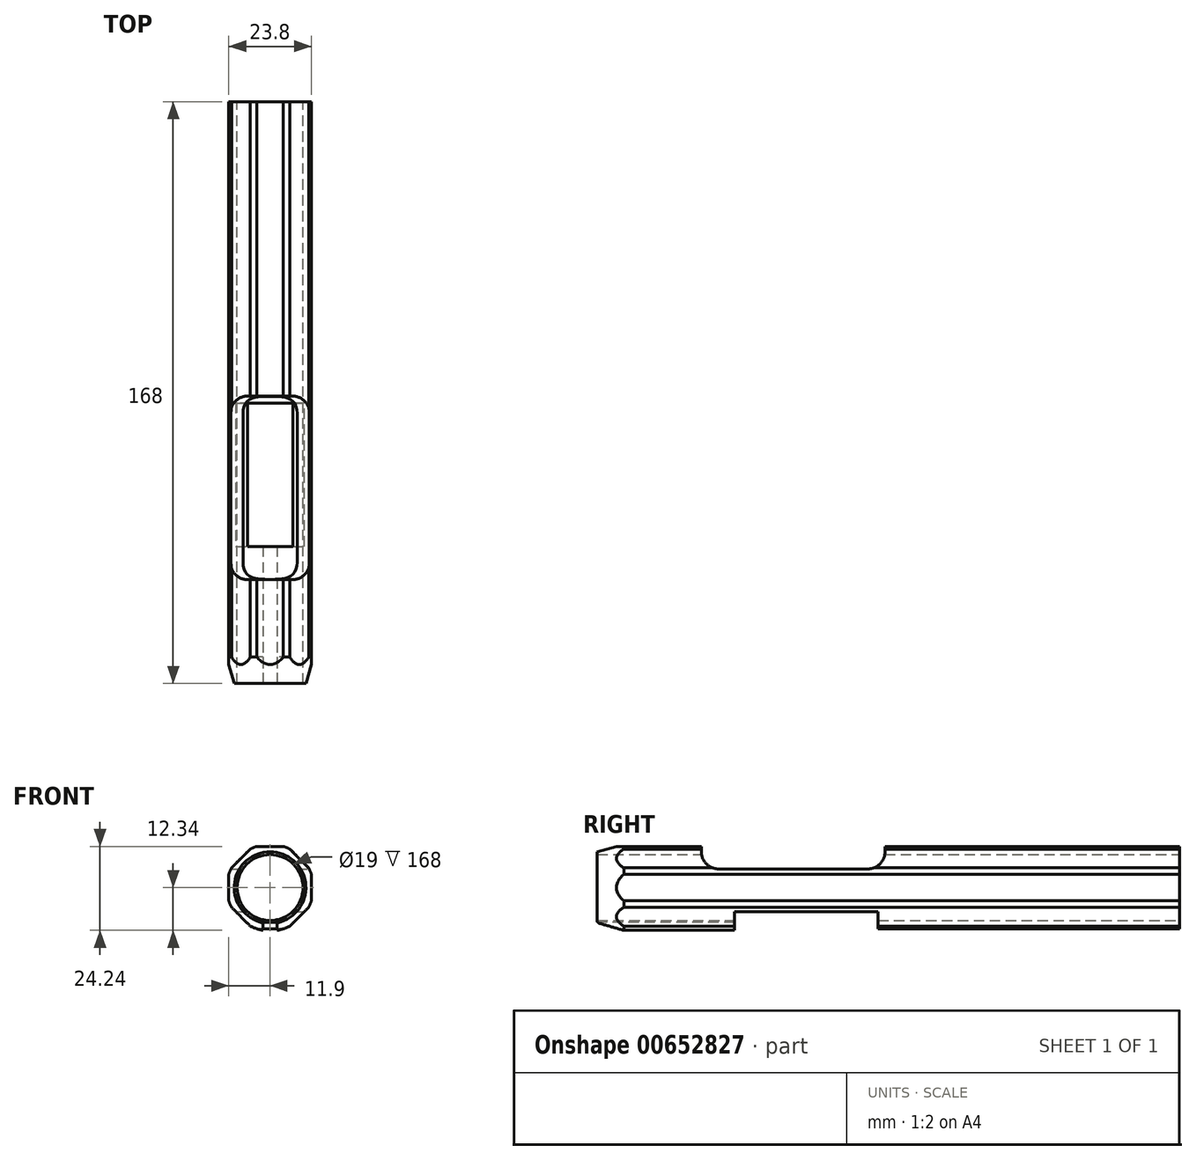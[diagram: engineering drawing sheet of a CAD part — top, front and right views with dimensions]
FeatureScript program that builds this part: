
annotation { "Feature Type Name" : "Feature", "Feature Type Description" : "" }
export const myFeature = defineFeature(function(context is Context, id is Id, definition is map)
    precondition{}
    {
        {
            var Q0;
            Q0=qCreatedBy(makeId("Front.planeOp"),FACE);
            var sketch = newSketch(context, id + "F0", { "sketchPlane" : qUnion([Q0])});
            skArc(sketch, "E0", {"start": v(-11.9, -3.84) * mm, "mid": v(-11.55, -4.78) * mm, "end": v(-11.13, -5.7) * mm});
            skLineSegment(sketch, "E1.0", {"start": v(11.9, 3.84) * mm, "end": v(11.9, -3.84) * mm});
            skLineSegment(sketch, "E1.1", {"start": v(11.13, -5.7) * mm, "end": v(5.7, -11.13) * mm});
            skLineSegment(sketch, "E1.2", {"start": v(3.84, -11.9) * mm, "end": v(-3.84, -11.9) * mm});
            skLineSegment(sketch, "E1.3", {"start": v(-5.7, -11.13) * mm, "end": v(-11.13, -5.7) * mm});
            skLineSegment(sketch, "E1.4", {"start": v(-11.9, -3.84) * mm, "end": v(-11.9, 3.84) * mm});
            skLineSegment(sketch, "E1.5", {"start": v(-11.13, 5.7) * mm, "end": v(-5.7, 11.13) * mm});
            skLineSegment(sketch, "E1.6", {"start": v(-3.84, 11.9) * mm, "end": v(3.84, 11.9) * mm});
            skLineSegment(sketch, "E1.7", {"start": v(5.7, 11.13) * mm, "end": v(11.13, 5.7) * mm});
            skPoint(sketch, "E1.0.midPoint", {"position": v(11.9, 0) * mm});
            skPoint(sketch, "E2.orphan", {"position": v(11.9, 4.93) * mm});
            skPoint(sketch, "E3.orphan", {"position": v(11.9, -4.93) * mm});
            skArc(sketch, "E4.trimOffspring", {"start": v(-11.13, 5.7) * mm, "mid": v(-11.55, 4.78) * mm, "end": v(-11.9, 3.84) * mm});
            skArc(sketch, "E5.trimOffspring", {"start": v(-3.84, 11.9) * mm, "mid": v(-4.78, 11.55) * mm, "end": v(-5.7, 11.13) * mm});
            skArc(sketch, "E6.trimOffspring", {"start": v(5.7, 11.13) * mm, "mid": v(4.78, 11.55) * mm, "end": v(3.84, 11.9) * mm});
            skArc(sketch, "E7.trimOffspring", {"start": v(11.9, 3.84) * mm, "mid": v(11.55, 4.78) * mm, "end": v(11.13, 5.7) * mm});
            skArc(sketch, "E8.trimOffspring", {"start": v(11.13, -5.7) * mm, "mid": v(11.55, -4.78) * mm, "end": v(11.9, -3.84) * mm});
            skArc(sketch, "E9.trimOffspring", {"start": v(3.84, -11.9) * mm, "mid": v(4.78, -11.55) * mm, "end": v(5.7, -11.13) * mm});
            skArc(sketch, "E10.trimOffspring", {"start": v(-5.7, -11.13) * mm, "mid": v(-4.78, -11.55) * mm, "end": v(-3.84, -11.9) * mm});
            skCircle(sketch, "E11", {"center": v(0, 0) * mm, "radius": 9.5 * mm});
            skSolve(sketch);
        }
        {
            var Q0;
            Q0 = qSketchRegion(id + "F0", true);
            extrude(context, id + "F1", {"entities" : qUnion([Q0]), "endBound" : BoundingType.SYMMETRIC, "depth" : 168 * mm, "offsetDistance" : 25 * mm});
        }
        {
            var Q0;
            Q0=qCreatedBy(makeId("Right.planeOp"),FACE);
            var sketch = newSketch(context, id + "F2", { "sketchPlane" : qUnion([Q0])});
            skLineSegment(sketch, "E12.0", {"start": v(-84, 11.13) * mm, "end": v(-84, 5.7) * mm, "construction": true});
            skLineSegment(sketch, "E13", {"start": v(-84, 11.13) * mm, "end": v(-84, -33.45) * mm, "construction": true});
            skLineSegment(sketch, "E14", {"start": v(-84, -33.45) * mm, "end": v(-84, 32.17) * mm, "construction": true});
            skLineSegment(sketch, "E15.bottom", {"start": v(-54, 23.3) * mm, "end": v(-1, 23.3) * mm});
            skLineSegment(sketch, "E15.top", {"start": v(-49, 5.4) * mm, "end": v(-6, 5.4) * mm});
            skLineSegment(sketch, "E15.left", {"start": v(-54, 23.3) * mm, "end": v(-54, 10.4) * mm});
            skLineSegment(sketch, "E15.right", {"start": v(-1, 23.3) * mm, "end": v(-1, 10.4) * mm});
            skLineSegment(sketch, "E16.0", {"start": v(-84, 11.9) * mm, "end": v(84, 11.9) * mm, "construction": true});
            skPoint(sketch, "E17", {"position": v(-54, 11.9) * mm});
            skPoint(sketch, "E18", {"position": v(-1, 11.9) * mm});
            skPoint(sketch, "E19.visualSharp", {"position": v(-54, 5.4) * mm});
            skArc(sketch, "E19.filletArc", {"start": v(-54, 10.4) * mm, "mid": v(-52.54, 6.86) * mm, "end": v(-49, 5.4) * mm});
            skPoint(sketch, "E20.visualSharp", {"position": v(-1, 5.4) * mm});
            skArc(sketch, "E20.filletArc", {"start": v(-6, 5.4) * mm, "mid": v(-2.46, 6.86) * mm, "end": v(-1, 10.4) * mm});
            skSolve(sketch);
        }
        {
            var Q0;
            Q0 = qSketchRegion(id + "F2", true);
            extrude(context, id + "F3", {"entities" : qUnion([Q0]), "operationType" : NewBodyOperationType.REMOVE, "endBound" : BoundingType.SYMMETRIC, "oppositeDirection" : true, "depth" : 25 * mm, "offsetDistance" : 25 * mm});
        }
        {
            var Q0;
            Q0=qCreatedBy(makeId("Right.planeOp"),FACE);
            var sketch = newSketch(context, id + "F4", { "sketchPlane" : qUnion([Q0])});
            skLineSegment(sketch, "E21.0", {"start": v(-84, -11.9) * mm, "end": v(84, -11.9) * mm, "construction": true});
            skLineSegment(sketch, "E22.0", {"start": v(-84, -5.7) * mm, "end": v(-84, -11.13) * mm, "construction": true});
            skLineSegment(sketch, "E23.0", {"start": v(-84, -11.9) * mm, "end": v(-84, -11.13) * mm, "construction": true});
            skLineSegment(sketch, "E24", {"start": v(-44.4, -11.9) * mm, "end": v(-44.4, -23.5) * mm});
            skPoint(sketch, "E25", {"position": v(-44.4, -11.9) * mm});
            skLineSegment(sketch, "E26", {"start": v(-44.4, -11.9) * mm, "end": v(-44.4, -6.9) * mm});
            skLineSegment(sketch, "E27", {"start": v(-44.4, -6.9) * mm, "end": v(-3, -6.9) * mm});
            skLineSegment(sketch, "E28", {"start": v(-3, -6.9) * mm, "end": v(-3, -23.5) * mm});
            skLineSegment(sketch, "E29", {"start": v(-3, -23.5) * mm, "end": v(-44.4, -23.5) * mm});
            skSolve(sketch);
        }
        {
            var Q0;
            Q0 = qSketchRegion(id + "F4", true);
            extrude(context, id + "F5", {"entities" : qUnion([Q0]), "operationType" : NewBodyOperationType.REMOVE, "endBound" : BoundingType.SYMMETRIC, "oppositeDirection" : true, "depth" : 25 * mm, "offsetDistance" : 25 * mm});
        }
        {
            var Q0;
            Q0=makeQuery(id+"F1.opExtrude","CAP_FACE",FACE,{"disambiguationData":[OSD([sQuery(id+"F0.wireOp",EDGE,"E0"),sQuery(id+"F0.wireOp",EDGE,"E1.0"),sQuery(id+"F0.wireOp",EDGE,"E1.1"),sQuery(id+"F0.wireOp",EDGE,"E1.2"),sQuery(id+"F0.wireOp",EDGE,"E1.3"),sQuery(id+"F0.wireOp",EDGE,"E1.4"),sQuery(id+"F0.wireOp",EDGE,"E1.5"),sQuery(id+"F0.wireOp",EDGE,"E1.6"),sQuery(id+"F0.wireOp",EDGE,"E1.7"),sQuery(id+"F0.wireOp",EDGE,"E4.trimOffspring"),sQuery(id+"F0.wireOp",EDGE,"E5.trimOffspring"),sQuery(id+"F0.wireOp",EDGE,"E6.trimOffspring"),sQuery(id+"F0.wireOp",EDGE,"E7.trimOffspring"),sQuery(id+"F0.wireOp",EDGE,"E8.trimOffspring"),sQuery(id+"F0.wireOp",EDGE,"E9.trimOffspring"),sQuery(id+"F0.wireOp",EDGE,"E10.trimOffspring"),sQuery(id+"F0.wireOp",EDGE,"E11")])],"isStart":false});
            cPlane(context, id + "F6", {"entities" : qUnion([Q0]), "cplaneType" : CPlaneType.OFFSET, "offset" : 0 * mm, "width" : 150 * mm, "height" : 150 * mm});
        }
        {
            var Q0;
            Q0=qCreatedBy(id+"F6.planeOp",FACE);
            var sketch = newSketch(context, id + "F7", { "sketchPlane" : qUnion([Q0])});
            skLineSegment(sketch, "E30.0", {"start": v(3.84, -11.9) * mm, "end": v(-3.84, -11.9) * mm, "construction": true});
            skCircle(sketch, "E31.0", {"center": v(0, 0) * mm, "radius": 9.5 * mm, "construction": true});
            skLineSegment(sketch, "E32.bottom", {"start": v(-2, -10) * mm, "end": v(2, -10) * mm});
            skLineSegment(sketch, "E32.top", {"start": v(-2, -13.8) * mm, "end": v(2, -13.8) * mm});
            skLineSegment(sketch, "E32.left", {"start": v(-2, -10) * mm, "end": v(-2, -13.8) * mm});
            skLineSegment(sketch, "E32.right", {"start": v(2, -10) * mm, "end": v(2, -13.8) * mm});
            skPoint(sketch, "E32.middle", {"position": v(0, -11.9) * mm});
            skArc(sketch, "E33", {"start": v(-3.84, -11.9) * mm, "mid": v(0, -12.5) * mm, "end": v(3.84, -11.9) * mm, "construction": true});
            skArc(sketch, "E34.0", {"start": v(-5.7, -11.13) * mm, "mid": v(-4.78, -11.55) * mm, "end": v(-3.84, -11.9) * mm, "construction": true});
            skPoint(sketch, "E35", {"position": v(0, -12.5) * mm});
            skSolve(sketch);
        }
        {
            var Q0;
            Q0 = qSketchRegion(id + "F7", true);
            extrude(context, id + "F8", {"entities" : qUnion([Q0]), "operationType" : NewBodyOperationType.REMOVE, "oppositeDirection" : true, "depth" : 50.14 * mm, "offsetDistance" : 25 * mm});
        }
        {
            var Q0;
            Q0=qCreatedBy(id+"F6.planeOp",FACE);
            var sketch = newSketch(context, id + "F9", { "sketchPlane" : qUnion([Q0])});
            skLineSegment(sketch, "E36.0", {"start": v(-2, -11.9) * mm, "end": v(-3.84, -11.9) * mm, "construction": true});
            skArc(sketch, "E37.0", {"start": v(-5.7, -11.13) * mm, "mid": v(-4.78, -11.55) * mm, "end": v(-3.84, -11.9) * mm, "construction": true});
            skLineSegment(sketch, "E38.0", {"start": v(-2, -10) * mm, "end": v(-2, -11.9) * mm, "construction": true});
            skLineSegment(sketch, "E39.0", {"start": v(-2, -10) * mm, "end": v(2, -10) * mm, "construction": true});
            skLineSegment(sketch, "E40.0", {"start": v(2, -10) * mm, "end": v(2, -11.9) * mm, "construction": true});
            skLineSegment(sketch, "E41.0", {"start": v(3.84, -11.9) * mm, "end": v(2, -11.9) * mm, "construction": true});
            skArc(sketch, "E42.0", {"start": v(3.84, -11.9) * mm, "mid": v(4.78, -11.55) * mm, "end": v(5.7, -11.13) * mm, "construction": true});
            skArc(sketch, "E43", {"start": v(-3.84, -11.9) * mm, "mid": v(-2.93, -12.15) * mm, "end": v(-2, -12.34) * mm});
            skLineSegment(sketch, "E44", {"start": v(2, -10) * mm, "end": v(2, -12.34) * mm});
            skLineSegment(sketch, "E45", {"start": v(-2, -11.9) * mm, "end": v(-2, -12.34) * mm});
            skLineSegment(sketch, "E46", {"start": v(2, -11.9) * mm, "end": v(3.84, -11.9) * mm});
            skLineSegment(sketch, "E47", {"start": v(-2, -11.9) * mm, "end": v(-3.84, -11.9) * mm});
            skArc(sketch, "E48.trimOffspring", {"start": v(2, -12.34) * mm, "mid": v(2.93, -12.15) * mm, "end": v(3.84, -11.9) * mm});
            skSolve(sketch);
        }
        {
            var Q0;
            Q0 = qSketchRegion(id + "F9", true);
            var Q1;
            Q1=makeQuery(id+"F5.boolean.opBoolean","COPY",FACE,{"derivedFrom":makeQuery(id+"F5.opExtrude","SWEPT_FACE",FACE,{"disambiguationData":[OSD([sQuery(id+"F4.wireOp",EDGE,"E24"),sQuery(id+"F4.wireOp",EDGE,"E26")])]})});
            extrude(context, id + "F10", {"entities" : qUnion([Q0]), "operationType" : NewBodyOperationType.ADD, "endBound" : BoundingType.UP_TO_SURFACE, "oppositeDirection" : true, "depth" : 25 * mm, "endBoundEntityFace" : qUnion([Q1]), "offsetDistance" : 25 * mm});
        }
        {
            var Q0;
            Q0=qCreatedBy(makeId("Right.planeOp"),FACE);
            var sketch = newSketch(context, id + "F11", { "sketchPlane" : qUnion([Q0])});
            skLineSegment(sketch, "E49.0.0", {"start": v(-44.4, -12.34) * mm, "end": v(-44.4, -11.13) * mm, "construction": true});
            skLineSegment(sketch, "E49.0.1", {"start": v(-44.4, -11.13) * mm, "end": v(-84, -11.13) * mm, "construction": true});
            skLineSegment(sketch, "E49.0.2", {"start": v(-84, -11.13) * mm, "end": v(-84, -12.34) * mm, "construction": true});
            skLineSegment(sketch, "E49.0.3", {"start": v(-84, -12.34) * mm, "end": v(-44.4, -12.34) * mm, "construction": true});
            skLineSegment(sketch, "E50", {"start": v(-84, -12.34) * mm, "end": v(-81.5, -12.34) * mm});
            skLineSegment(sketch, "E51", {"start": v(-84, -12.34) * mm, "end": v(-84, -9.84) * mm});
            skLineSegment(sketch, "E52", {"start": v(-84, -9.84) * mm, "end": v(-81.5, -12.34) * mm});
            skLineSegment(sketch, "E53", {"start": v(-81.5, -12.34) * mm, "end": v(-84, -12.34) * mm});
            skSolve(sketch);
        }
        {
            var Q0;
            Q0 = qSketchRegion(id + "F11", true);
            extrude(context, id + "F12", {"entities" : qUnion([Q0]), "operationType" : NewBodyOperationType.REMOVE, "endBound" : BoundingType.SYMMETRIC, "oppositeDirection" : true, "depth" : 25 * mm, "offsetDistance" : 25 * mm});
        }
        {
            var Q0;
            Q0=qCreatedBy(makeId("Right.planeOp"),FACE);
            var sketch = newSketch(context, id + "F13", { "sketchPlane" : qUnion([Q0])});
            skLineSegment(sketch, "E54", {"start": v(0, 0) * mm, "end": v(-102.11, 0) * mm, "construction": true});
            skPoint(sketch, "E55.0", {"position": v(-84, -9.84) * mm});
            skLineSegment(sketch, "E56", {"start": v(-84, -12.34) * mm, "end": v(-84.65, -12.34) * mm, "construction": true});
            skPoint(sketch, "E57", {"position": v(-84, -12.34) * mm});
            skLineSegment(sketch, "E58", {"start": v(-67.19, -15.1) * mm, "end": v(-86.8, -19.09) * mm});
            skLineSegment(sketch, "E59", {"start": v(-84, -12.34) * mm, "end": v(-84, -10.34) * mm, "construction": true});
            skPoint(sketch, "E60.0.start.orphan", {"position": v(-44.4, -12.34) * mm});
            skPoint(sketch, "E61.end.orphan", {"position": v(-76, -12.34) * mm});
            skPoint(sketch, "E61.start.orphan", {"position": v(-81.5, -12.34) * mm});
            skLineSegment(sketch, "E62", {"start": v(-84, -10.34) * mm, "end": v(-67.19, -15.1) * mm});
            skLineSegment(sketch, "E63", {"start": v(-84, -10.34) * mm, "end": v(-86.8, -19.09) * mm});
            skSolve(sketch);
        }
        {
            var Q0;
            Q0 = qSketchRegion(id + "F13", true);
            var Q1;
            Q1=sQuery(id+"F13.wireOp",EDGE,"E54");
            revolve(context, id + "F14", {"operationType" : NewBodyOperationType.REMOVE, "entities" : qUnion([Q0]), "axis" : qUnion([Q1]), "revolveType" : RevolveType.FULL, "oppositeDirection" : true});
        }
    });
